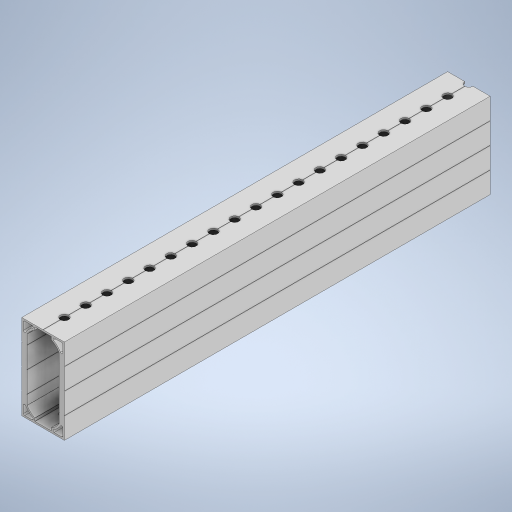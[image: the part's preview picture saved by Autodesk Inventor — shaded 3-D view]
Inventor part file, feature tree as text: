
AUTODESK INVENTOR PART (.ipt)
format: ipt  version: 2023.4 (Build 274418000, 418)  size: 782,848 bytes
history: native  units: in
note: dims shown in document units (in); Inventor stores cm internally (conversion verified against a paired STEP export)
features: extrude x1, sketch x1, other x1
ambient origin geometry x8: Origin, YZ Plane, XZ Plane, XY Plane, X Axis, Y Axis, Z Axis, Center Point
bodies: Solid1 (feature_tree)
feature tree (3):
  extrude  "Extrusion1"  [1 undecoded]
  sketch  "Sketch1"  dims[d0=37.0in d1=0.0in]
  other  "Internal Fillets"
note: 1 required parameter value undecoded (feature->parameter linkage not recoverable at this tier; creation-order binding heuristic only, values carry confidence <= 0.55)
